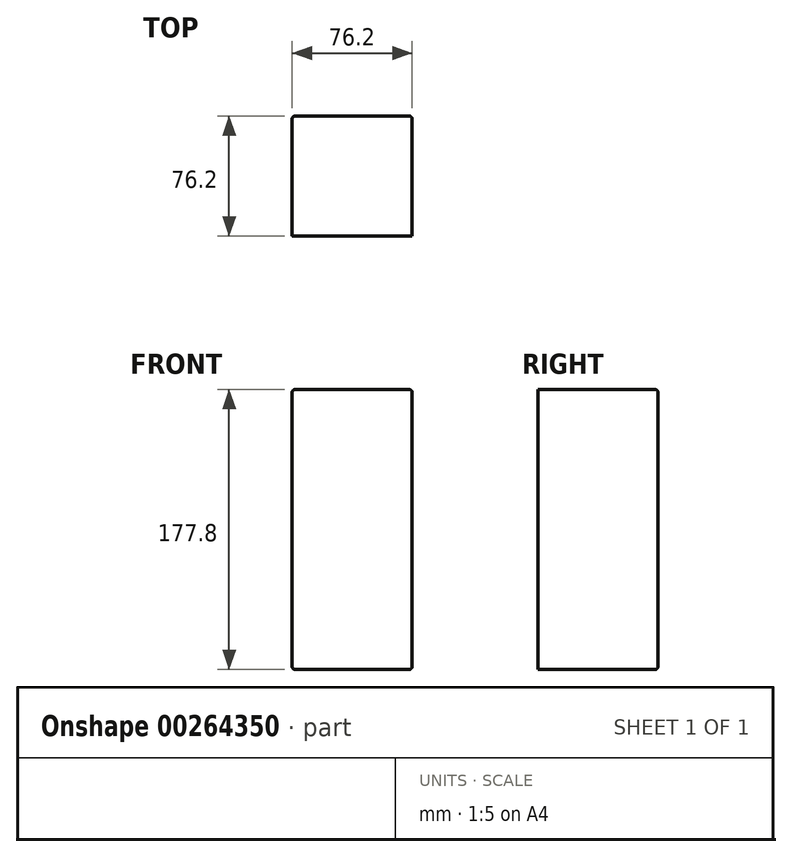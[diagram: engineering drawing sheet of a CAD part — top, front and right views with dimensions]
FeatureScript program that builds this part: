
annotation { "Feature Type Name" : "Feature", "Feature Type Description" : "" }
export const myFeature = defineFeature(function(context is Context, id is Id, definition is map)
    precondition{}
    {
        {
            var Q0;
            Q0=qCreatedBy(makeId("Front.planeOp"),FACE);
            var sketch = newSketch(context, id + "F0", { "sketchPlane" : qUnion([Q0])});
            skLineSegment(sketch, "E0.bottom", {"start": v(38.1, -88.9) * mm, "end": v(-38.1, -88.9) * mm});
            skLineSegment(sketch, "E0.top", {"start": v(38.1, 88.9) * mm, "end": v(-38.1, 88.9) * mm});
            skLineSegment(sketch, "E0.left", {"start": v(38.1, -88.9) * mm, "end": v(38.1, 88.9) * mm});
            skLineSegment(sketch, "E0.right", {"start": v(-38.1, -88.9) * mm, "end": v(-38.1, 88.9) * mm});
            skPoint(sketch, "E0.middle", {"position": v(0, 0) * mm});
            skSolve(sketch);
        }
        {
            var Q0;
            Q0 = qSketchRegion(id + "F0", true);
            extrude(context, id + "F1", {"entities" : qUnion([Q0]), "oppositeDirection" : true, "depth" : 76.2 * mm});
        }
        {
            var Q0;
            Q0=makeQuery(id+"F1.opExtrude","CAP_FACE",FACE,{"disambiguationData":[OSD([sQuery(id+"F0.wireOp",EDGE,"E0.bottom"),sQuery(id+"F0.wireOp",EDGE,"E0.top"),sQuery(id+"F0.wireOp",EDGE,"E0.left"),sQuery(id+"F0.wireOp",EDGE,"E0.right")])],"isStart":false});
            var Q1;
            Q1=makeQuery(id+"F1.opExtrude","SWEPT_EDGE",EDGE,{"disambiguationData":[OSD([sQuery(id+"F0.wireOp",EDGE,"E0.top"),sQuery(id+"F0.wireOp",EDGE,"E0.left")])]});
            var Q2;
            Q2=makeQuery(id+"F1.opExtrude","SWEPT_EDGE",EDGE,{"disambiguationData":[OSD([sQuery(id+"F0.wireOp",EDGE,"E0.top"),sQuery(id+"F0.wireOp",EDGE,"E0.right")])]});
            var Q3;
            Q3=makeQuery(id+"F1.opExtrude","SWEPT_EDGE",EDGE,{"disambiguationData":[OSD([sQuery(id+"F0.wireOp",EDGE,"E0.bottom"),sQuery(id+"F0.wireOp",EDGE,"E0.left")])]});
            var Q4;
            Q4=makeQuery(id+"F1.opExtrude","SWEPT_EDGE",EDGE,{"disambiguationData":[OSD([sQuery(id+"F0.wireOp",EDGE,"E0.bottom"),sQuery(id+"F0.wireOp",EDGE,"E0.right")])]});
            fillet(context, id + "F2", {"entities" : qUnion([Q0, Q1, Q2, Q3, Q4]), "radius" : 1.9 * mm, "tangentPropagation" : true, "allowEdgeOverflow" : false});
        }
    });
